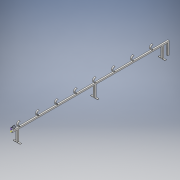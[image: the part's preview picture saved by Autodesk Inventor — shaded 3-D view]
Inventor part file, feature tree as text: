
AUTODESK INVENTOR PART (.ipt)
format: ipt  version: 2017 (Build 210142000, 142)  size: 232,448 bytes
history: native  units: mm
features: sketch x8, extrude x7, pattern_linear x3
ambient origin geometry x8: Origin, YZ Plane, XZ Plane, XY Plane, X Axis, Y Axis, Z Axis, Center Point
bodies: Solid1 (feature_tree)
feature tree (18):
  extrude  "Extrusion1"  Depth=2800.0mm
  extrude  "Extrusion2"  Depth=25.0mm
  extrude  "Extrusion5"  Depth=5.0mm
  extrude  "Extrusion6"  Depth=50.0mm TaperAngle=0.0deg
  extrude  "Extrusion7"  Depth=50.0mm TaperAngle=0.0deg
  pattern_linear  "Rectangular Pattern3"  Count1=8 Spacing1=338.0mm
  sketch  "Sketch10"  dims[d31=4.0mm]
  extrude  "Extrusion8"  Depth=290.0mm
  pattern_linear  "Rectangular Pattern4"  Spacing1=42.0mm  [1 undecoded]
  pattern_linear  "Rectangular Pattern5"  Spacing1=25.0mm  [1 undecoded]
  extrude  "Extrusion9"  Depth=25.0mm
  sketch  "Sketch1"  dims[d0=25.0mm d1=2800.0mm]
  sketch  "Sketch2"  dims[d2=25.0mm d3=0.0mm d4=25.0mm]
  sketch  "Sketch6"  dims[d5=200.0mm d6=0.0mm d13=5.0mm]
  sketch  "Sketch7"  dims[d14=25.0mm d15=50.0mm d16=75.0mm d17=0.0mm d18=0.0mm]
  sketch  "Sketch8"  dims[d22=5.0mm d23=50.0mm d24=75.0mm d25=0.0mm d26=0.0mm]
  sketch  "Sketch11"  dims[d32=25.0mm d33=0.0mm d34=80.0mm d36=338.0mm]
  sketch  "Sketch12"  dims[d39=42.0mm d40=290.0mm d41=42.0mm d42=25.0mm d43=25.0mm d44=10.0mm d45=0.0mm d46=20.0mm d48=1204.0mm d49=0.0mm d50=20.0mm d52=1379.0mm d53=25.0mm d54=25.0mm d55=0.0mm d56=10.0mm d57=0.0mm]
note: 2 required parameter values undecoded (feature->parameter linkage not recoverable at this tier; creation-order binding heuristic only, values carry confidence <= 0.55)
